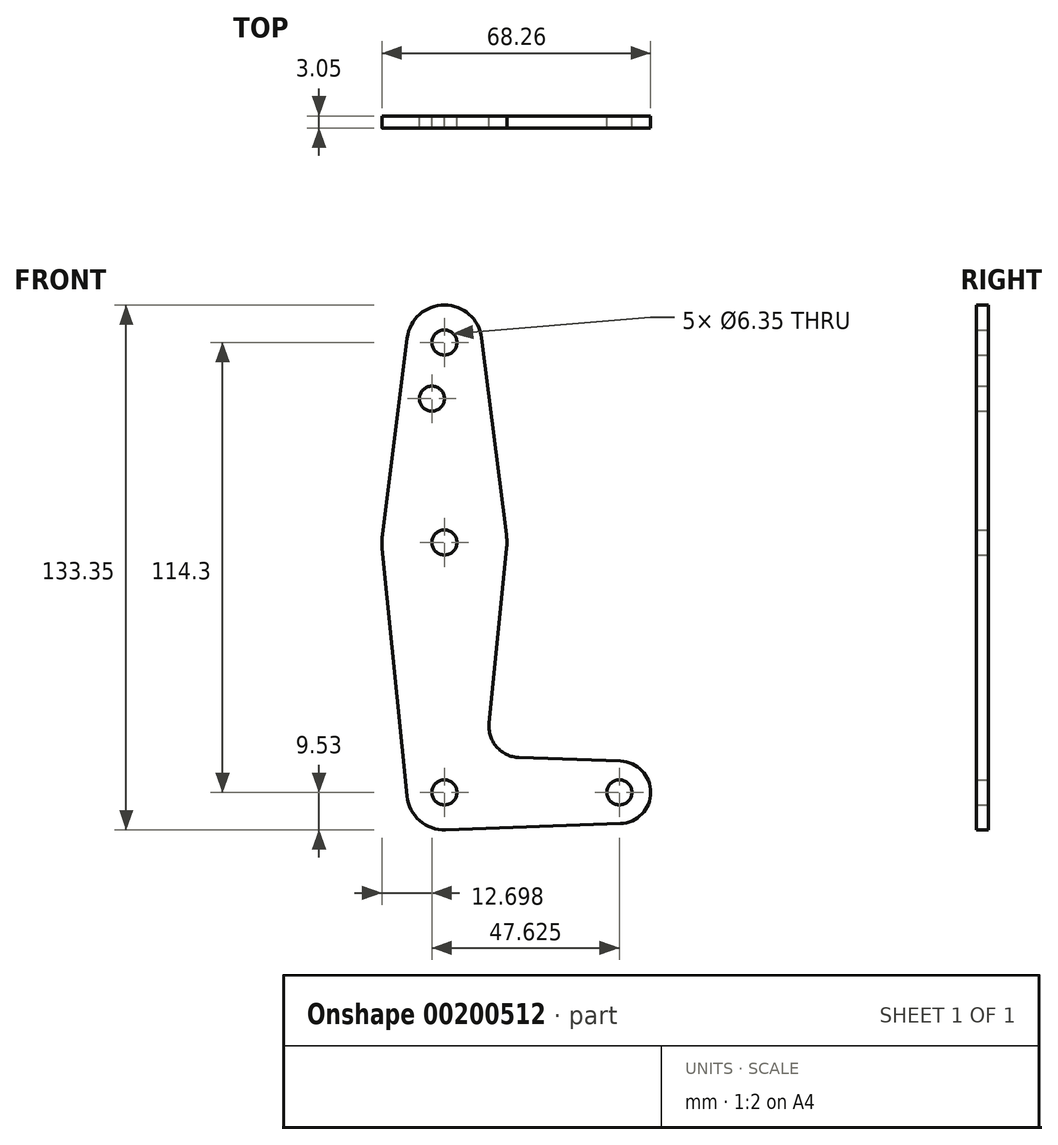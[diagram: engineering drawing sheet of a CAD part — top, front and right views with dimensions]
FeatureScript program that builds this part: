
annotation { "Feature Type Name" : "Feature", "Feature Type Description" : "" }
export const myFeature = defineFeature(function(context is Context, id is Id, definition is map)
    precondition{}
    {
        {
            var Q0;
            Q0=qCreatedBy(makeId("Front.planeOp"),FACE);
            var sketch = newSketch(context, id + "F0", { "sketchPlane" : qUnion([Q0])});
            skLineSegment(sketch, "E0", {"start": v(-67.82, 81.12) * mm, "end": v(-67.82, -33.18) * mm, "construction": true});
            skLineSegment(sketch, "E1", {"start": v(-67.82, -33.18) * mm, "end": v(-23.37, -33.18) * mm, "construction": true});
            skCircle(sketch, "E2", {"center": v(-67.82, 81.12) * mm, "radius": 9.53 * mm});
            skCircle(sketch, "E3", {"center": v(-67.82, 30.32) * mm, "radius": 15.88 * mm});
            skCircle(sketch, "E4", {"center": v(-67.82, -33.18) * mm, "radius": 9.53 * mm});
            skCircle(sketch, "E5", {"center": v(-23.37, -33.18) * mm, "radius": 7.94 * mm});
            skLineSegment(sketch, "E6", {"start": v(-77.27, 82.31) * mm, "end": v(-83.57, 32.3) * mm});
            skLineSegment(sketch, "E7", {"start": v(-83.61, 28.73) * mm, "end": v(-77.3, -34.13) * mm});
            skLineSegment(sketch, "E8", {"start": v(-58.37, 82.31) * mm, "end": v(-52.07, 32.3) * mm});
            skLineSegment(sketch, "E9", {"start": v(-52.02, 28.73) * mm, "end": v(-56.48, -15.59) * mm});
            skLineSegment(sketch, "E10", {"start": v(-67.48, -42.7) * mm, "end": v(-23.08, -41.11) * mm});
            skLineSegment(sketch, "E11", {"start": v(-48.85, -24.33) * mm, "end": v(-23.08, -25.25) * mm});
            skCircle(sketch, "E12", {"center": v(-71, 66.85) * mm, "radius": 3.18 * mm});
            skCircle(sketch, "E13", {"center": v(-67.82, 81.12) * mm, "radius": 3.18 * mm});
            skCircle(sketch, "E14", {"center": v(-67.82, -33.18) * mm, "radius": 3.18 * mm});
            skCircle(sketch, "E15", {"center": v(-23.37, -33.18) * mm, "radius": 3.18 * mm});
            skCircle(sketch, "E16", {"center": v(-67.82, 30.32) * mm, "radius": 3.18 * mm});
            skArc(sketch, "E17.filletArc", {"start": v(-56.48, -15.59) * mm, "mid": v(-54.56, -21.6) * mm, "end": v(-48.85, -24.33) * mm});
            skSolve(sketch);
        }
        {
            var Q0;
            Q0=makeQuery(id+"F0.imprint","IMPRINT",FACE,{"disambiguationData":[TD([[makeQuery(id+"F0.imprint","IMPRINT",EDGE,{"derivedFrom":sQuery(id+"F0.wireOp",EDGE,"E13")}),-1.0]])]});
            var Q1;
            {var subQ1=sQuery(id+"F0.wireOp",EDGE,"E6");Q1=makeQuery(id+"F0.imprint","IMPRINT",FACE,{"disambiguationData":[TD([[makeQuery(id+"F0.imprint","IMPRINT",EDGE,{"derivedFrom":subQ1}),1.0]])]});}
            var Q2;
            Q2=makeQuery(id+"F0.imprint","IMPRINT",FACE,{"disambiguationData":[TD([[makeQuery(id+"F0.imprint","IMPRINT",EDGE,{"derivedFrom":sQuery(id+"F0.wireOp",EDGE,"E16")}),-1.0]])]});
            var Q3;
            {var subQ0=sQuery(id+"F0.wireOp",EDGE,"E7");Q3=makeQuery(id+"F0.imprint","IMPRINT",FACE,{"disambiguationData":[TD([[makeQuery(id+"F0.imprint","IMPRINT",EDGE,{"derivedFrom":subQ0}),1.0]])]});}
            var Q4;
            Q4=makeQuery(id+"F0.imprint","IMPRINT",FACE,{"disambiguationData":[TD([[makeQuery(id+"F0.imprint","IMPRINT",EDGE,{"derivedFrom":sQuery(id+"F0.wireOp",EDGE,"E14")}),-1.0]])]});
            var Q5;
            Q5=makeQuery(id+"F0.imprint","IMPRINT",FACE,{"disambiguationData":[TD([[makeQuery(id+"F0.imprint","IMPRINT",EDGE,{"derivedFrom":sQuery(id+"F0.wireOp",EDGE,"E15")}),-1.0]])]});
            extrude(context, id + "F1", {"entities" : qUnion([Q0, Q1, Q2, Q3, Q4, Q5]), "depth" : 3.05 * mm});
        }
    });
